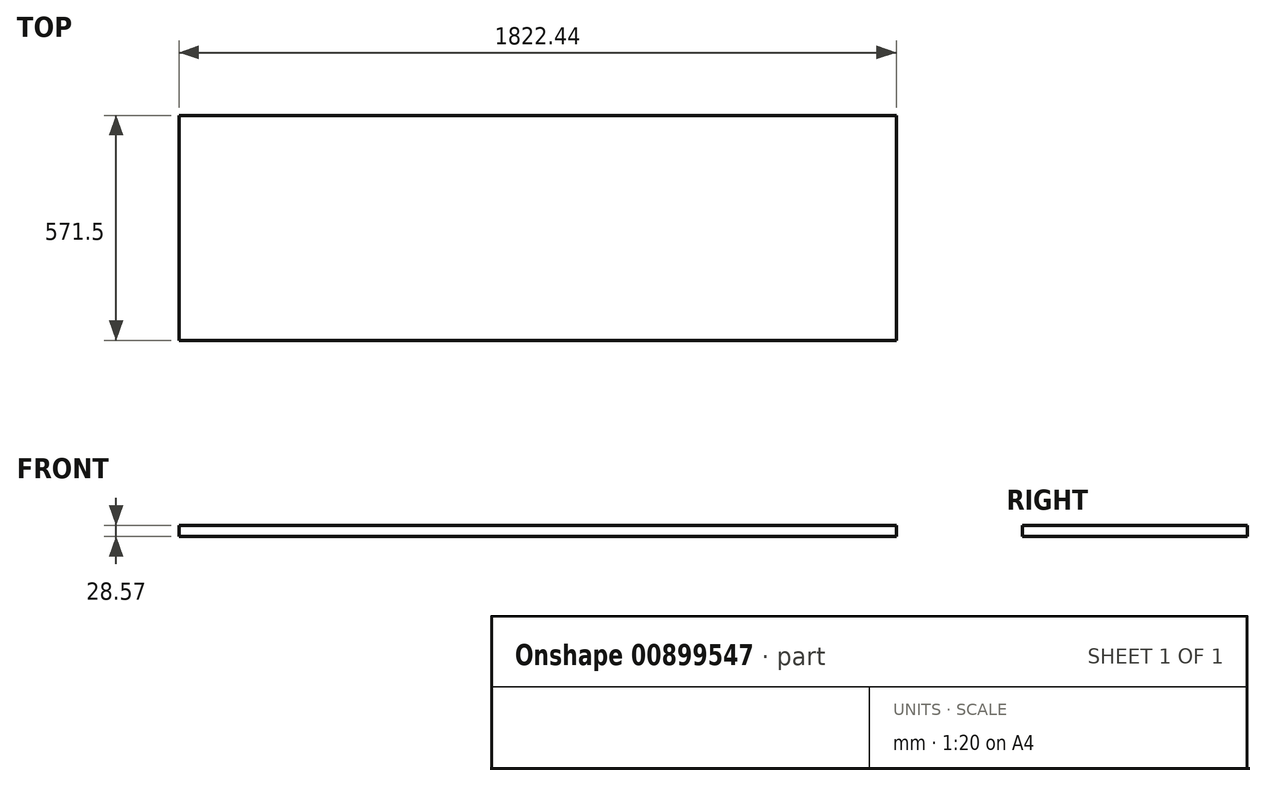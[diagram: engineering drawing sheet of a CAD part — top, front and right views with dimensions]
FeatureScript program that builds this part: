
annotation { "Feature Type Name" : "Feature", "Feature Type Description" : "" }
export const myFeature = defineFeature(function(context is Context, id is Id, definition is map)
    precondition{}
    {
        {
            var Q0;
            Q0=qCreatedBy(makeId("Top.planeOp"),FACE);
            var sketch = newSketch(context, id + "F0", { "sketchPlane" : qUnion([Q0])});
            skLineSegment(sketch, "E0.bottom", {"start": v(-911.23, 285.75) * mm, "end": v(911.23, 285.75) * mm});
            skLineSegment(sketch, "E0.top", {"start": v(-911.23, -285.75) * mm, "end": v(911.22, -285.75) * mm});
            skLineSegment(sketch, "E0.left", {"start": v(-911.23, 285.75) * mm, "end": v(-911.23, -285.75) * mm});
            skLineSegment(sketch, "E0.right", {"start": v(911.23, 285.75) * mm, "end": v(911.22, -285.75) * mm});
            skPoint(sketch, "E0.middle", {"position": v(0, 0) * mm});
            skSolve(sketch);
        }
        {
            var Q0;
            Q0=makeQuery(id+"F0.imprint","IMPRINT",FACE,{"disambiguationData":[TD([[makeQuery(id+"F0.imprint","IMPRINT",EDGE,{"derivedFrom":sQuery(id+"F0.wireOp",EDGE,"E0.bottom")}),-1.0]])]});
            extrude(context, id + "F1", {"entities" : qUnion([Q0]), "depth" : 28.57 * mm, "offsetDistance" : 25.4 * mm});
        }
    });
